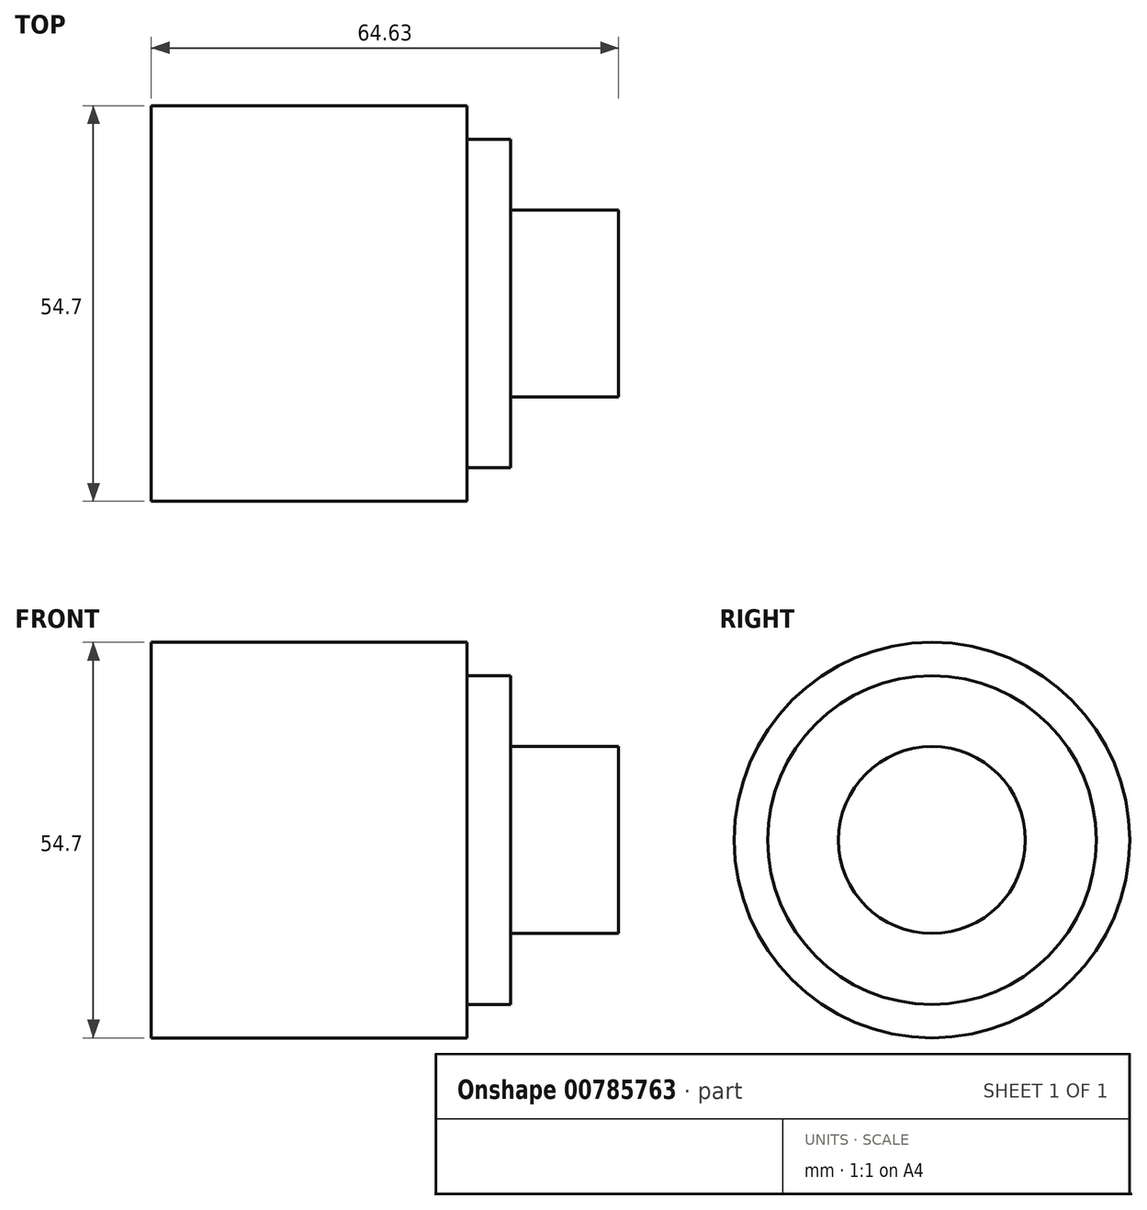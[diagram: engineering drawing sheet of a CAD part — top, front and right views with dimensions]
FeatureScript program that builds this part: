
annotation { "Feature Type Name" : "Feature", "Feature Type Description" : "" }
export const myFeature = defineFeature(function(context is Context, id is Id, definition is map)
    precondition{}
    {
        {
            var Q0;
            Q0=qCreatedBy(makeId("Front.planeOp"),FACE);
            var sketch = newSketch(context, id + "F0", { "sketchPlane" : qUnion([Q0])});
            skLineSegment(sketch, "E0", {"start": v(0, 0) * mm, "end": v(0, 27.35) * mm});
            skLineSegment(sketch, "E1", {"start": v(0, 27.35) * mm, "end": v(43.68, 27.35) * mm});
            skLineSegment(sketch, "E2", {"start": v(43.68, 27.35) * mm, "end": v(43.68, 22.72) * mm});
            skLineSegment(sketch, "E3", {"start": v(43.68, 22.72) * mm, "end": v(49.67, 22.72) * mm});
            skLineSegment(sketch, "E4", {"start": v(49.67, 22.72) * mm, "end": v(49.67, 12.93) * mm});
            skLineSegment(sketch, "E5", {"start": v(49.67, 12.93) * mm, "end": v(64.63, 12.93) * mm});
            skLineSegment(sketch, "E6", {"start": v(64.63, 12.93) * mm, "end": v(64.63, 0) * mm});
            skLineSegment(sketch, "E7", {"start": v(64.63, 0) * mm, "end": v(0, 0) * mm});
            skSolve(sketch);
        }
        {
            var Q0;
            Q0=makeQuery(id+"F0.imprint","IMPRINT",FACE,{"disambiguationData":[TD([[makeQuery(id+"F0.imprint","IMPRINT",EDGE,{"derivedFrom":sQuery(id+"F0.wireOp",EDGE,"E0")}),-1.0]])]});
            var Q1;
            Q1=sQuery(id+"F0.wireOp",EDGE,"E7");
            revolve(context, id + "F1", {"surfaceOperationType" : NewSurfaceOperationType.NEW, "entities" : qUnion([Q0]), "axis" : qUnion([Q1]), "revolveType" : RevolveType.FULL});
        }
    });
